# Revit family: Котел_ТЕРМОТЕХНИК_ТТ250_ 322-1940 кВт
name_source: partatom
category: Оборудование
units: mm (PartAtom-declared; Revit-internal decimal feet)

## family parameters
Всегда вертикально = Да
Классификация = Нет
На основе рабочей плоскости = Нет
Общий = Нет
При загрузке вырезать с полостями = Нет
Размер круглого соединителя = Использовать диаметр
Тип детали = Нормальный
Точка расчета площади = Нет

## types (12) — shared parameters
G = 25 мм
URL = https://www.entroros.ru
Видимость_ВКЛ = Да
Видимость_ВЫКЛ = Нет
Изготовитель = ЭНТРОРОС
Ключевая пометка = https://www.entroros.ru
Код по классификатору = D3020100
Материал_Условный BOX = <По категории>
Описание = Котел ЭНТРОРОС ТЕРМОТЕХНИК ТТ250
Производитель = ЭНТРОРОС
Семейство заказано = ООО ЭНТРОРОС (entroros.ru)
Семейство оборудования = ТТ250
Семейство разработано = ООО DASBIM (dasbim.ru)
Ссылка на документацию = https://www.entroros.ru
Штуцер_Вход воды_D = 40 мм
Штуцер_Датчик дым.газов_D = G1/2-B
Штуцер_Непрер.продувка_D = 20 мм
Штуцер_Период. продувка_D = 50 мм
Штуцер_Пред.клапан_С = 200 мм
Штуцер_Слив воды_D = 50 мм
Штуцер_Слив воды_D_Формула = G1/2-B
Штуцер_Слив конденсата_D = 25 мм
Штуцер_Слив конденсата_D_Формула = G1-B
Штуцер_Тягонапоромер_D = G1/2-B
zero-valued in all types: Стоимость

## per-type parameters (varying)
- 0.5_322_0.8_ef_633-01: B=1340 мм; H=1884 мм; L=2538 мм; А_Дверь_Смещение наружной грани=2413 мм; Аэродин. сопротивление (Па)=279; Давление (мПа)=0.80; Дверь_633=Да; Дверь_635=Нет; Дверь_6361=Нет; Дверь_638=Нет; КПД (%)=88.7; Комментарии к типоразмеру=322 кВт; Корпус_633=Да; Корпус_635=Нет; Корпус_6361=Нет; Корпус_638=Нет; Масса наполненного котла (кг)=3111; Масса сухого котла (кг)=2255; Ном. мощность (кВт)=322; Паропроизводительность (т/ч)=0.5; С_Ось котла=880 мм; Штуцер_Вход воды_В=1130 мм; Штуцер_Вход воды_С=269 мм; Штуцер_Выход дыма_D=211 мм; Штуцер_Выход дыма_В=930 мм; Штуцер_Выход пара_D=50 мм; Штуцер_Выход пара_А=1084 мм; Штуцер_Выход пара_В=1650 мм; Штуцер_Горелка_D=180 мм; Штуцер_Горелка_В=662 мм; Штуцер_Период. продувка_А=1114 мм; Штуцер_Пред.клапан_D=20 мм; Штуцер_Пред.клапан_А=446 мм; Штуцер_Слив воды_А=690 мм; Штуцер_Слив воды_В=148 мм; Штуцер_Слив воды_С=600 мм; Штуцер_Слив конденсата_В=327 мм
- 0.5_324_1.2_ef_633: B=1340 мм; H=1884 мм; L=2538 мм; А_Дверь_Смещение наружной грани=2413 мм; Аэродин. сопротивление (Па)=286; Давление (мПа)=1.20; Дверь_633=Да; Дверь_635=Нет; Дверь_6361=Нет; Дверь_638=Нет; КПД (%)=88.0; Комментарии к типоразмеру=324 кВт; Корпус_633=Да; Корпус_635=Нет; Корпус_6361=Нет; Корпус_638=Нет; Масса наполненного котла (кг)=3111; Масса сухого котла (кг)=2255; Ном. мощность (кВт)=324; Паропроизводительность (т/ч)=0.5; С_Ось котла=880 мм; Штуцер_Вход воды_В=1130 мм; Штуцер_Вход воды_С=269 мм; Штуцер_Выход дыма_D=211 мм; Штуцер_Выход дыма_В=930 мм; Штуцер_Выход пара_D=50 мм; Штуцер_Выход пара_А=1084 мм; Штуцер_Выход пара_В=1650 мм; Штуцер_Горелка_D=180 мм; Штуцер_Горелка_В=662 мм; Штуцер_Период. продувка_А=1114 мм; Штуцер_Пред.клапан_D=20 мм; Штуцер_Пред.клапан_А=446 мм; Штуцер_Слив воды_А=690 мм; Штуцер_Слив воды_В=148 мм; Штуцер_Слив воды_С=600 мм; Штуцер_Слив конденсата_В=327 мм
- 1.0_643_0.8_ef_635-01: B=1677 мм; H=2131 мм; L=3102 мм; А_Дверь_Смещение наружной грани=2979 мм; Аэродин. сопротивление (Па)=394; Давление (мПа)=0.80; Дверь_633=Нет; Дверь_635=Да; Дверь_6361=Нет; Дверь_638=Нет; КПД (%)=90.9; Комментарии к типоразмеру=634 кВт; Корпус_633=Нет; Корпус_635=Да; Корпус_6361=Нет; Корпус_638=Нет; Масса наполненного котла (кг)=5812; Масса сухого котла (кг)=4007; Ном. мощность (кВт)=643; Паропроизводительность (т/ч)=1.0; С_Ось котла=1048 мм; Штуцер_Вход воды_В=1387 мм; Штуцер_Вход воды_С=312 мм; Штуцер_Выход дыма_D=300 мм; Штуцер_Выход дыма_В=1122 мм; Штуцер_Выход пара_D=80 мм; Штуцер_Выход пара_А=1175 мм; Штуцер_Выход пара_В=1989 мм; Штуцер_Горелка_D=280 мм; Штуцер_Горелка_В=772 мм; Штуцер_Период. продувка_А=1680 мм; Штуцер_Пред.клапан_D=25 мм; Штуцер_Пред.клапан_А=446 мм; Штуцер_Слив воды_А=690 мм; Штуцер_Слив воды_В=148 мм; Штуцер_Слив воды_С=600 мм; Штуцер_Слив конденсата_В=325 мм
- 1.0_647_1.2_ef_635: B=1677 мм; H=2131 мм; L=3102 мм; А_Дверь_Смещение наружной грани=2979 мм; Аэродин. сопротивление (Па)=408; Давление (мПа)=1.20; Дверь_633=Нет; Дверь_635=Да; Дверь_6361=Нет; Дверь_638=Нет; КПД (%)=90.1; Комментарии к типоразмеру=647 кВт; Корпус_633=Нет; Корпус_635=Да; Корпус_6361=Нет; Корпус_638=Нет; Масса наполненного котла (кг)=5812; Масса сухого котла (кг)=4007; Ном. мощность (кВт)=647; Паропроизводительность (т/ч)=1.0; С_Ось котла=1048 мм; Штуцер_Вход воды_В=1387 мм; Штуцер_Вход воды_С=312 мм; Штуцер_Выход дыма_D=300 мм; Штуцер_Выход дыма_В=1122 мм; Штуцер_Выход пара_D=80 мм; Штуцер_Выход пара_А=1175 мм; Штуцер_Выход пара_В=1989 мм; Штуцер_Горелка_D=280 мм; Штуцер_Горелка_В=772 мм; Штуцер_Период. продувка_А=1680 мм; Штуцер_Пред.клапан_D=25 мм; Штуцер_Пред.клапан_А=446 мм; Штуцер_Слив воды_А=690 мм; Штуцер_Слив воды_В=148 мм; Штуцер_Слив воды_С=600 мм; Штуцер_Слив конденсата_В=325 мм
- 1.5_965_0.8_ef_635-01: B=1677 мм; H=2131 мм; L=3102 мм; А_Дверь_Смещение наружной грани=2979 мм; Аэродин. сопротивление (Па)=736; Давление (мПа)=0.80; Дверь_633=Нет; Дверь_635=Да; Дверь_6361=Нет; Дверь_638=Нет; КПД (%)=89.5; Комментарии к типоразмеру=965 кВт; Корпус_633=Нет; Корпус_635=Да; Корпус_6361=Нет; Корпус_638=Нет; Масса наполненного котла (кг)=6044; Масса сухого котла (кг)=4128; Ном. мощность (кВт)=965; Паропроизводительность (т/ч)=1.5; С_Ось котла=1048 мм; Штуцер_Вход воды_В=1387 мм; Штуцер_Вход воды_С=312 мм; Штуцер_Выход дыма_D=300 мм; Штуцер_Выход дыма_В=1122 мм; Штуцер_Выход пара_D=80 мм; Штуцер_Выход пара_А=1175 мм; Штуцер_Выход пара_В=1989 мм; Штуцер_Горелка_D=280 мм; Штуцер_Горелка_В=772 мм; Штуцер_Период. продувка_А=1680 мм; Штуцер_Пред.клапан_D=25 мм; Штуцер_Пред.клапан_А=446 мм; Штуцер_Слив воды_А=690 мм; Штуцер_Слив воды_В=148 мм; Штуцер_Слив воды_С=600 мм; Штуцер_Слив конденсата_В=325 мм
- 1.5_971_1.2_ef_635: B=1677 мм; H=2131 мм; L=3102 мм; А_Дверь_Смещение наружной грани=2979 мм; Аэродин. сопротивление (Па)=764; Давление (мПа)=1.20; Дверь_633=Нет; Дверь_635=Да; Дверь_6361=Нет; Дверь_638=Нет; КПД (%)=88.7; Комментарии к типоразмеру=971 кВт; Корпус_633=Нет; Корпус_635=Да; Корпус_6361=Нет; Корпус_638=Нет; Масса наполненного котла (кг)=6044; Масса сухого котла (кг)=4128; Ном. мощность (кВт)=971; Паропроизводительность (т/ч)=1.5; С_Ось котла=1048 мм; Штуцер_Вход воды_В=1387 мм; Штуцер_Вход воды_С=312 мм; Штуцер_Выход дыма_D=300 мм; Штуцер_Выход дыма_В=1122 мм; Штуцер_Выход пара_D=80 мм; Штуцер_Выход пара_А=1175 мм; Штуцер_Выход пара_В=1989 мм; Штуцер_Горелка_D=280 мм; Штуцер_Горелка_В=772 мм; Штуцер_Период. продувка_А=1680 мм; Штуцер_Пред.клапан_D=25 мм; Штуцер_Пред.клапан_А=446 мм; Штуцер_Слив воды_А=690 мм; Штуцер_Слив воды_В=148 мм; Штуцер_Слив воды_С=600 мм; Штуцер_Слив конденсата_В=325 мм
- 2.0_1287_0.8_ef_6361-01: B=1820 мм; H=2281 мм; L=3406 мм; А_Дверь_Смещение наружной грани=3283 мм; Аэродин. сопротивление (Па)=689; Давление (мПа)=0.80; Дверь_633=Нет; Дверь_635=Нет; Дверь_6361=Да; Дверь_638=Нет; КПД (%)=89.9; Комментарии к типоразмеру=1287 кВт; Корпус_633=Нет; Корпус_635=Нет; Корпус_6361=Да; Корпус_638=Нет; Масса наполненного котла (кг)=7516; Масса сухого котла (кг)=5168; Ном. мощность (кВт)=1287; Паропроизводительность (т/ч)=2.0; С_Ось котла=1118 мм; Штуцер_Вход воды_В=1541 мм; Штуцер_Вход воды_С=312 мм; Штуцер_Выход дыма_D=350 мм; Штуцер_Выход дыма_В=1251 мм; Штуцер_Выход пара_D=80 мм; Штуцер_Выход пара_А=1538 мм; Штуцер_Выход пара_В=2132 мм; Штуцер_Горелка_D=280 мм; Штуцер_Горелка_В=849 мм; Штуцер_Период. продувка_А=1978 мм; Штуцер_Пред.клапан_D=32 мм; Штуцер_Пред.клапан_А=450 мм; Штуцер_Слив воды_А=692 мм; Штуцер_Слив воды_В=148 мм; Штуцер_Слив воды_С=646 мм; Штуцер_Слив конденсата_В=325 мм
- 2.0_1294_1.2_ef_6361: B=1820 мм; H=2281 мм; L=3406 мм; А_Дверь_Смещение наружной грани=3283 мм; Аэродин. сопротивление (Па)=715; Давление (мПа)=1.20; Дверь_633=Нет; Дверь_635=Нет; Дверь_6361=Да; Дверь_638=Нет; КПД (%)=89.1; Комментарии к типоразмеру=1294 кВт; Корпус_633=Нет; Корпус_635=Нет; Корпус_6361=Да; Корпус_638=Нет; Масса наполненного котла (кг)=7516; Масса сухого котла (кг)=5168; Ном. мощность (кВт)=1294; Паропроизводительность (т/ч)=2.0; С_Ось котла=1118 мм; Штуцер_Вход воды_В=1541 мм; Штуцер_Вход воды_С=312 мм; Штуцер_Выход дыма_D=350 мм; Штуцер_Выход дыма_В=1251 мм; Штуцер_Выход пара_D=80 мм; Штуцер_Выход пара_А=1538 мм; Штуцер_Выход пара_В=2132 мм; Штуцер_Горелка_D=280 мм; Штуцер_Горелка_В=849 мм; Штуцер_Период. продувка_А=1978 мм; Штуцер_Пред.клапан_D=32 мм; Штуцер_Пред.клапан_А=450 мм; Штуцер_Слив воды_А=692 мм; Штуцер_Слив воды_В=148 мм; Штуцер_Слив воды_С=646 мм; Штуцер_Слив конденсата_В=325 мм
- 2.5_1608_0.8_ef_637-01: B=1820 мм; H=2281 мм; L=3406 мм; А_Дверь_Смещение наружной грани=3283 мм; Аэродин. сопротивление (Па)=1016; Давление (мПа)=0.80; Дверь_633=Нет; Дверь_635=Нет; Дверь_6361=Да; Дверь_638=Нет; КПД (%)=88.9; Комментарии к типоразмеру=1608 кВт; Корпус_633=Нет; Корпус_635=Нет; Корпус_6361=Да; Корпус_638=Нет; Масса наполненного котла (кг)=7816; Масса сухого котла (кг)=5375; Ном. мощность (кВт)=1608; Паропроизводительность (т/ч)=2.5; С_Ось котла=1118 мм; Штуцер_Вход воды_В=1541 мм; Штуцер_Вход воды_С=312 мм; Штуцер_Выход дыма_D=350 мм; Штуцер_Выход дыма_В=1251 мм; Штуцер_Выход пара_D=80 мм; Штуцер_Выход пара_А=1538 мм; Штуцер_Выход пара_В=2132 мм; Штуцер_Горелка_D=280 мм; Штуцер_Горелка_В=849 мм; Штуцер_Период. продувка_А=1978 мм; Штуцер_Пред.клапан_D=32 мм; Штуцер_Пред.клапан_А=450 мм; Штуцер_Слив воды_А=692 мм; Штуцер_Слив воды_В=148 мм; Штуцер_Слив воды_С=646 мм; Штуцер_Слив конденсата_В=325 мм
- 2.5_1618_1.2_ef_637: B=1820 мм; H=2281 мм; L=3406 мм; А_Дверь_Смещение наружной грани=3283 мм; Аэродин. сопротивление (Па)=1054; Давление (мПа)=1.20; Дверь_633=Нет; Дверь_635=Нет; Дверь_6361=Да; Дверь_638=Нет; КПД (%)=88.1; Комментарии к типоразмеру=1618 кВт; Корпус_633=Нет; Корпус_635=Нет; Корпус_6361=Да; Корпус_638=Нет; Масса наполненного котла (кг)=7816; Масса сухого котла (кг)=5375; Ном. мощность (кВт)=1618; Паропроизводительность (т/ч)=2.5; С_Ось котла=1118 мм; Штуцер_Вход воды_В=1541 мм; Штуцер_Вход воды_С=312 мм; Штуцер_Выход дыма_D=350 мм; Штуцер_Выход дыма_В=1251 мм; Штуцер_Выход пара_D=80 мм; Штуцер_Выход пара_А=1538 мм; Штуцер_Выход пара_В=2132 мм; Штуцер_Горелка_D=280 мм; Штуцер_Горелка_В=849 мм; Штуцер_Период. продувка_А=1978 мм; Штуцер_Пред.клапан_D=32 мм; Штуцер_Пред.клапан_А=450 мм; Штуцер_Слив воды_А=692 мм; Штуцер_Слив воды_В=148 мм; Штуцер_Слив воды_С=646 мм; Штуцер_Слив конденсата_В=325 мм
- 3.0_1930_0.8_ef_638-01: B=1978 мм; H=2386 мм; L=3718 мм; А_Дверь_Смещение наружной грани=3595 мм; Аэродин. сопротивление (Па)=1133; Давление (мПа)=0.80; Дверь_633=Нет; Дверь_635=Нет; Дверь_6361=Нет; Дверь_638=Да; КПД (%)=89.7; Комментарии к типоразмеру=1930 кВт; Корпус_633=Нет; Корпус_635=Нет; Корпус_6361=Нет; Корпус_638=Да; Масса наполненного котла (кг)=9760; Масса сухого котла (кг)=6900; Ном. мощность (кВт)=1930; Паропроизводительность (т/ч)=3.0; С_Ось котла=1139 мм; Штуцер_Вход воды_В=1631 мм; Штуцер_Вход воды_С=312 мм; Штуцер_Выход дыма_D=350 мм; Штуцер_Выход дыма_В=1341 мм; Штуцер_Выход пара_D=100 мм; Штуцер_Выход пара_А=1596 мм; Штуцер_Выход пара_В=2232 мм; Штуцер_Горелка_D=280 мм; Штуцер_Горелка_В=864 мм; Штуцер_Период. продувка_А=2176 мм; Штуцер_Пред.клапан_D=32 мм; Штуцер_Пред.клапан_А=452 мм; Штуцер_Слив воды_А=692 мм; Штуцер_Слив воды_В=88 мм; Штуцер_Слив воды_С=750 мм; Штуцер_Слив конденсата_В=263 мм
- 3.0_1940_1.2_ef_638: B=1978 мм; H=2386 мм; L=3718 мм; А_Дверь_Смещение наружной грани=3595 мм; Аэродин. сопротивление (Па)=1180; Давление (мПа)=1.20; Дверь_633=Нет; Дверь_635=Нет; Дверь_6361=Нет; Дверь_638=Да; КПД (%)=88.9; Комментарии к типоразмеру=1940 кВт; Корпус_633=Нет; Корпус_635=Нет; Корпус_6361=Нет; Корпус_638=Да; Масса наполненного котла (кг)=9760; Масса сухого котла (кг)=6900; Ном. мощность (кВт)=1940; Паропроизводительность (т/ч)=3.0; С_Ось котла=1139 мм; Штуцер_Вход воды_В=1631 мм; Штуцер_Вход воды_С=312 мм; Штуцер_Выход дыма_D=350 мм; Штуцер_Выход дыма_В=1341 мм; Штуцер_Выход пара_D=100 мм; Штуцер_Выход пара_А=1596 мм; Штуцер_Выход пара_В=2232 мм; Штуцер_Горелка_D=280 мм; Штуцер_Горелка_В=864 мм; Штуцер_Период. продувка_А=2176 мм; Штуцер_Пред.клапан_D=32 мм; Штуцер_Пред.клапан_А=452 мм; Штуцер_Слив воды_А=692 мм; Штуцер_Слив воды_В=88 мм; Штуцер_Слив воды_С=750 мм; Штуцер_Слив конденсата_В=263 мм
